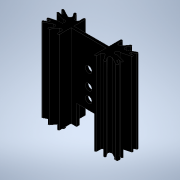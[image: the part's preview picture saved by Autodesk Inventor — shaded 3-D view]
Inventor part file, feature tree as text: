
AUTODESK INVENTOR PART (.ipt)
format: ipt  version: 2020.5 (Build 245400000, 400)  size: 214,016 bytes
history: native  units: mm
features: extrude x3, sketch x2
ambient origin geometry x8: Origin, YZ Plane, XZ Plane, XY Plane, X Axis, Y Axis, Z Axis, Center Point
bodies: Solid1 (feature_tree)
feature tree (5):
  sketch  "Sketch1"  dims[d22=38.0mm d23=0.0mm d24=8.0mm d25=4.0mm d26=0.0mm d27=0.0mm]
  extrude  "Extrusion1"  Depth=8.0mm TaperAngle=0.0deg
  extrude  "Extrusion2"  [1 undecoded]
  extrude  "Extrusion3"  [1 undecoded]
  sketch  "Sketch2"  dims[d37=5.686mm d38=0.0mm]
note: 2 required parameter values undecoded (feature->parameter linkage not recoverable at this tier; creation-order binding heuristic only, values carry confidence <= 0.55)
